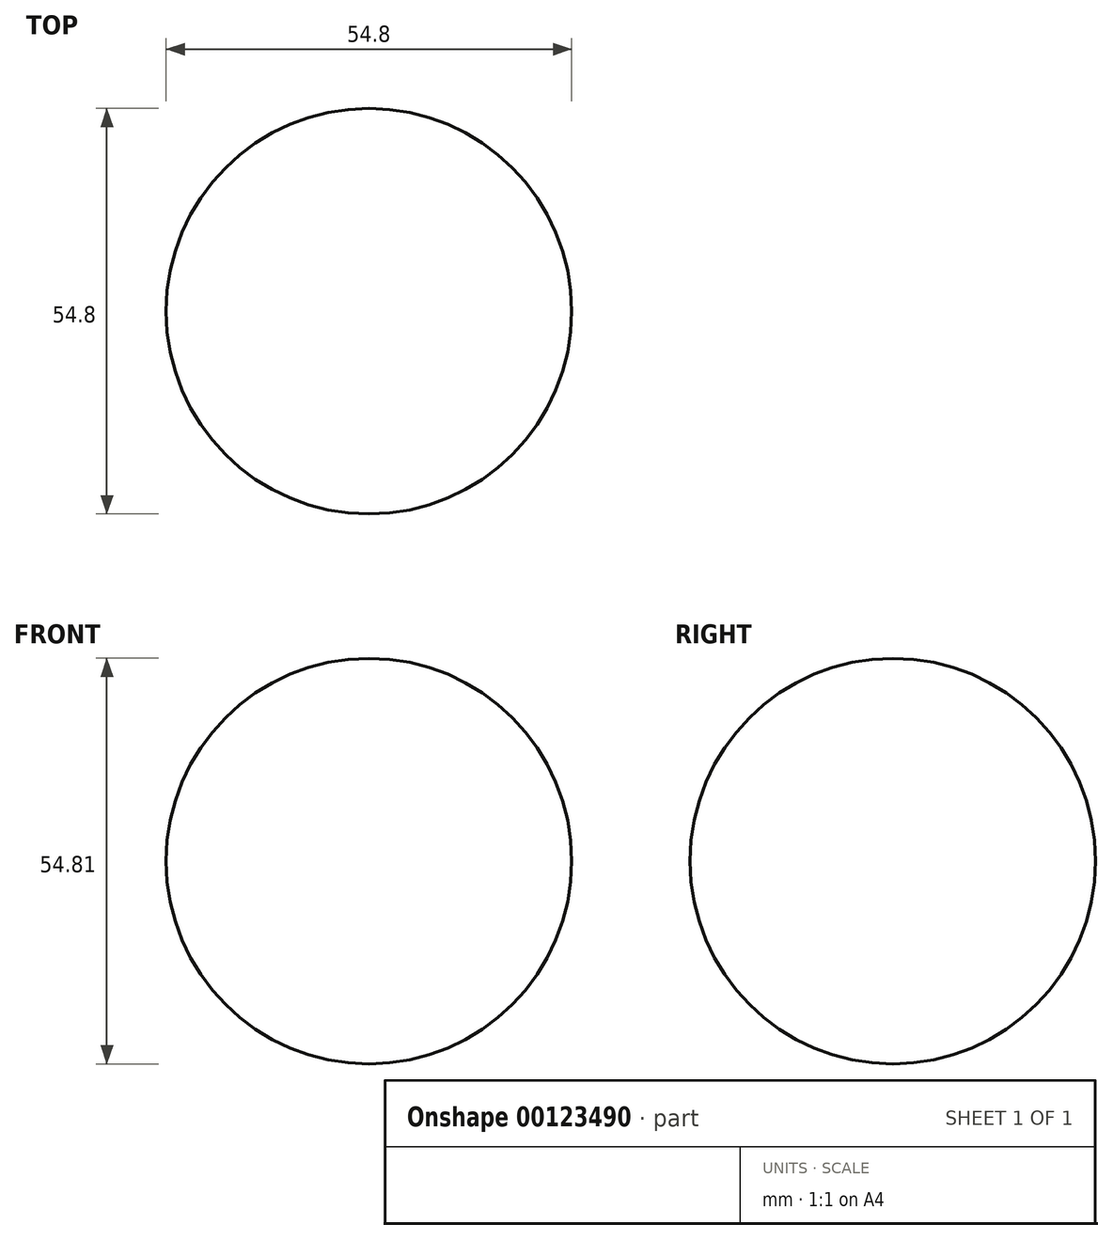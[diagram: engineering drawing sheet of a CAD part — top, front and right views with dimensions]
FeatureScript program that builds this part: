
annotation { "Feature Type Name" : "Feature", "Feature Type Description" : "" }
export const myFeature = defineFeature(function(context is Context, id is Id, definition is map)
    precondition{}
    {
        {
            var Q0;
            Q0=qCreatedBy(makeId("Front.planeOp"),FACE);
            var sketch = newSketch(context, id + "F0", { "sketchPlane" : qUnion([Q0])});
            skArc(sketch, "E0", {"start": v(0, 13.35) * mm, "mid": v(27.4, 40.75) * mm, "end": v(0, 68.16) * mm});
            skLineSegment(sketch, "E1", {"start": v(0, 13.35) * mm, "end": v(0, 68.16) * mm});
            skSolve(sketch);
        }
        {
            var Q0;
            Q0=makeQuery(id+"F0.imprint","IMPRINT",FACE,{"disambiguationData":[TD([[makeQuery(id+"F0.imprint","IMPRINT",EDGE,{"derivedFrom":sQuery(id+"F0.wireOp",EDGE,"E0")}),1.0]])]});
            var Q1;
            Q1=sQuery(id+"F0.wireOp",EDGE,"E1");
            revolve(context, id + "F1", {"entities" : qUnion([Q0]), "axis" : qUnion([Q1]), "revolveType" : RevolveType.FULL});
        }
    });
